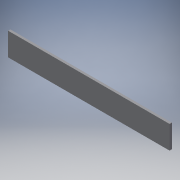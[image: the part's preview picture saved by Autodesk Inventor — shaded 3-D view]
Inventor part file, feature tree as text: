
AUTODESK INVENTOR PART (.ipt)
format: ipt  version: 2019 (Build 230136000, 136)  size: 103,424 bytes
history: native  units: mm
features: extrude x1, sketch x1
ambient origin geometry x8: Origin, YZ Plane, XZ Plane, XY Plane, X Axis, Y Axis, Z Axis, Center Point
bodies: Solid1 (feature_tree)
feature tree (2):
  extrude  "Extrusion1"  Depth=10.0mm
  sketch  "Sketch1"  dims[d0=500.0mm d1=10.0mm d2=500.0mm d3=100.0mm d4=200.0mm d5=100.0mm d6=10.0mm d7=0.0mm]
